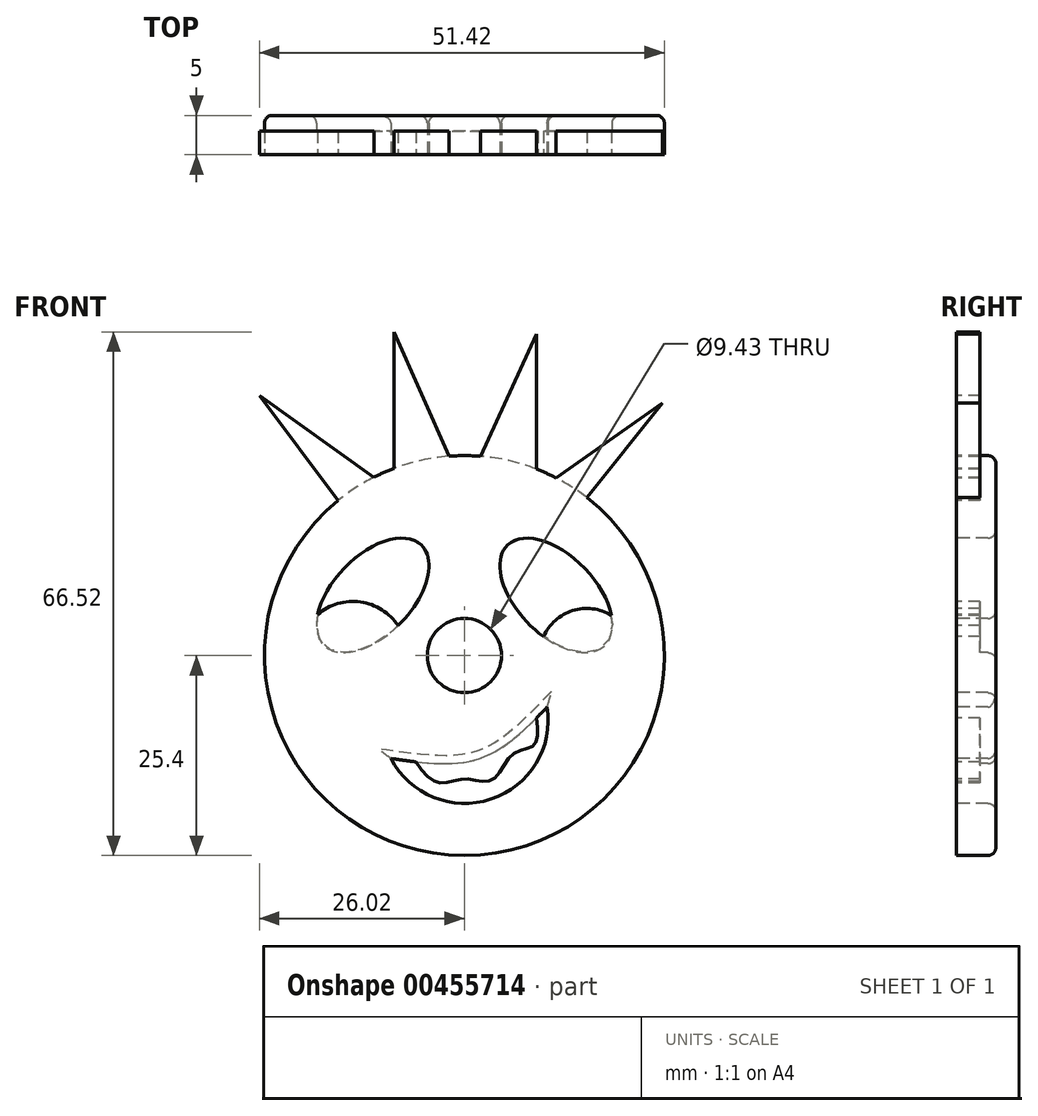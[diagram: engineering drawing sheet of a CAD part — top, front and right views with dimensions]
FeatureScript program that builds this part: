
annotation { "Feature Type Name" : "Feature", "Feature Type Description" : "" }
export const myFeature = defineFeature(function(context is Context, id is Id, definition is map)
    precondition{}
    {
        {
            var Q0;
            Q0=qCreatedBy(makeId("Front.planeOp"),FACE);
            var sketch = newSketch(context, id + "F0", { "sketchPlane" : qUnion([Q0])});
            skCircle(sketch, "E0", {"center": v(0, 0) * mm, "radius": 25.4 * mm});
            skSolve(sketch);
        }
        {
            var Q0;
            Q0 = qSketchRegion(id + "F0", true);
            var Q1;
            Q1 = qSketchRegion(id + "F2", true);
            extrude(context, id + "F1", {"entities" : qUnion([Q0, Q1]), "oppositeDirection" : true, "depth" : 5 * mm});
        }
        {
            var Q0;
            Q0=makeQuery(id+"F1.opExtrude","CAP_FACE",FACE,{"disambiguationData":[OSD([sQuery(id+"F0.wireOp",EDGE,"E0")])],"isStart":true});
            var sketch = newSketch(context, id + "F2", { "sketchPlane" : qUnion([Q0])});
            skEllipse(sketch, "E1", {"center": v(11.64, 7.65) * mm, "majorRadius": 8.88 * mm, "minorRadius": 5 * mm, "majorAxis": v(-0.7, 0.72)});
            skEllipse(sketch, "E2.MirrorC", {"center": v(-11.64, 7.65) * mm, "majorRadius": 8.88 * mm, "minorRadius": 5 * mm, "majorAxis": v(0.7, 0.72)});
            skArc(sketch, "E3", {"start": v(-9.33, -13.08) * mm, "mid": v(3.37, -18.24) * mm, "end": v(10.52, -6.54) * mm});
            skFitSpline(sketch, "E4", {"points": [v(-9.33, -13.08) * mm, v(1.95, -13.08) * mm, v(10.52, -6.54) * mm], "startDerivative": vector(23.55, -3.34) * mm, "endDerivative": vector(16.1, 16.5) * mm});
            skCircle(sketch, "E5", {"center": v(0, 0) * mm, "radius": 4.72 * mm});
            skSolve(sketch);
        }
        {
            var Q0;
            Q0 = qSketchRegion(id + "F2", true);
            extrude(context, id + "F3", {"entities" : qUnion([Q0]), "operationType" : NewBodyOperationType.REMOVE, "oppositeDirection" : true, "depth" : 5 * mm});
        }
        {
            var Q0;
            Q0=qCreatedBy(makeId("Front.planeOp"),FACE);
            var sketch = newSketch(context, id + "F4", { "sketchPlane" : qUnion([Q0])});
            skLineSegment(sketch, "E6", {"start": v(14.14, 18.22) * mm, "end": v(25.14, 32.06) * mm});
            skLineSegment(sketch, "E7", {"start": v(25.14, 32.06) * mm, "end": v(9.17, 20.83) * mm});
            skLineSegment(sketch, "E8", {"start": v(9.17, 20.83) * mm, "end": v(9.17, 40.84) * mm});
            skLineSegment(sketch, "E9", {"start": v(9.17, 40.84) * mm, "end": v(0, 20.83) * mm});
            skLineSegment(sketch, "E10", {"start": v(0, 20.83) * mm, "end": v(-8.95, 41.12) * mm});
            skLineSegment(sketch, "E11", {"start": v(-8.95, 41.12) * mm, "end": v(-8.95, 20.83) * mm});
            skLineSegment(sketch, "E12", {"start": v(-8.95, 20.83) * mm, "end": v(-26.02, 33.01) * mm});
            skLineSegment(sketch, "E13", {"start": v(-26.02, 33.01) * mm, "end": v(-13.7, 16.5) * mm});
            skLineSegment(sketch, "E14", {"start": v(-13.7, 16.5) * mm, "end": v(-6.59, 19.65) * mm});
            skLineSegment(sketch, "E15", {"start": v(-6.59, 19.65) * mm, "end": v(0.27, 16.5) * mm});
            skLineSegment(sketch, "E16", {"start": v(0.27, 16.5) * mm, "end": v(6.38, 19.2) * mm});
            skLineSegment(sketch, "E17", {"start": v(6.38, 19.2) * mm, "end": v(14.14, 18.22) * mm});
            skFitSpline(sketch, "E18", {"points": [v(8.9, -6.49) * mm, v(8.9, -11.3) * mm, v(6.2, -12.5) * mm, v(3.49, -15.82) * mm, v(0, -15.67) * mm, v(-3.43, -16.12) * mm, v(-7.35, -11.6) * mm], "startDerivative": vector(6.04, -33.33) * mm, "endDerivative": vector(-18.77, 30.94) * mm});
            skLineSegment(sketch, "E19", {"start": v(8.9, -6.49) * mm, "end": v(0, -11.6) * mm});
            skLineSegment(sketch, "E20", {"start": v(0, -11.6) * mm, "end": v(-7.35, -11.6) * mm});
            skCircle(sketch, "E21", {"center": v(15.54, 0) * mm, "radius": 5.99 * mm});
            skCircle(sketch, "E22", {"center": v(-14.14, 0) * mm, "radius": 6.88 * mm});
            skSolve(sketch);
        }
        {
            var Q0;
            Q0 = qSketchRegion(id + "F4", true);
            extrude(context, id + "F5", {"entities" : qUnion([Q0]), "operationType" : NewBodyOperationType.ADD, "oppositeDirection" : true, "depth" : 3 * mm});
        }
        {
            var Q0;
            Q0=makeQuery(id+"F1.opExtrude","CAP_FACE",FACE,{"disambiguationData":[OSD([sQuery(id+"F0.wireOp",EDGE,"E0")])],"isStart":false});
            fillet(context, id + "F6", {"entities" : qUnion([Q0]), "radius" : 1 * mm, "tangentPropagation" : true, "allowEdgeOverflow" : false});
        }
    });
